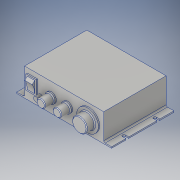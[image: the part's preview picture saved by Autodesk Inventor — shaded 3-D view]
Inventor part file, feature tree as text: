
AUTODESK INVENTOR PART (.ipt)
format: ipt  version: 2017 (Build 210142000, 142)  size: 264,192 bytes
history: native  units: in
note: dims shown in document units (in); Inventor stores cm internally (conversion verified against a paired STEP export)
features: projected_geometry x11, extrude x8, sketch x8, chamfer x2, plane x2, fillet x1
ambient origin geometry x8: Origin, YZ Plane, XZ Plane, XY Plane, X Axis, Y Axis, Z Axis, Center Point
bodies: Solid1 (feature_tree)
feature tree (32):
  extrude  "Extrusion1"  Depth=5.5118in
  extrude  "Extrusion2"  Depth=4.6063in
  fillet  "Fillet1"  Radius=1.5354in
  extrude  "Extrusion3"  Depth=1.2598in
  extrude  "Extrusion4"  Depth=0.5906in
  extrude  "Extrusion5"  Depth=0.5906in
  extrude  "Extrusion6"  Depth=0.1575in
  chamfer  "Chamfer1"  Distance=0.7874in
  chamfer  "Chamfer2"  Distance=0.5118in
  plane  "Work Plane1"
  plane  "Work Plane2"
  extrude  "Extrusion7"  Depth=1.2598in
  extrude  "Extrusion8"  Depth=0.5118in
  sketch  "Sketch1"  dims[d0=3.622in d1=5.5118in]
  sketch  "Sketch2"  dims[d2=0.0787in d3=0.0in d4=4.6063in d5=1.5354in d6=0.0in]
  projected_geometry  "Projected Loop1"
  sketch  "Sketch3"  dims[d7=0.0787in d8=1.2598in]
  projected_geometry  "Projected Loop2"
  sketch  "Sketch4"  dims[d9=0.5906in d10=0.5906in]
  projected_geometry  "Projected Loop3"
  projected_geometry  "Projected Loop4"
  projected_geometry  "Projected Loop5"
  projected_geometry  "Projected Loop6"
  sketch  "Sketch5"  dims[d11=0.2756in d12=0.5906in]
  projected_geometry  "Projected Loop7"
  sketch  "Sketch6"  dims[d13=0.8268in d14=0.1575in]
  projected_geometry  "Projected Loop8"
  sketch  "Sketch7"  dims[d15=0.2756in]
  projected_geometry  "Projected Loop9"
  sketch  "Sketch8"  dims[d17=0.3937in d18=0.7874in d19=0.5118in d20=1.2598in d21=0.5118in d22=2.2047in d23=0.1575in d24=0.2362in d25=0.0787in d26=0.0in d27=0.4921in d28=0.4921in d30=0.4921in d31=0.6181in d32=0.0in d33=0.8543in d34=0.5512in d35=0.0in d36=0.2598in d37=0.0in d38=0.0492in d39=0.0787in d40=45.0deg d41=0.0394in d42=0.0787in d43=45.0deg d44=-0.0787in d45=-0.0787in d46=0.0787in d47=0.0787in d48=45.0deg d49=0.1417in d50=0.2598in d51=0.0in d52=0.1693in d54=0.1693in d55=0.1693in d56=0.2756in d58=0.2756in d59=0.2756in d63=0.2598in d64=0.0in d66=0.1693in d67=0.2756in d68=0.9114in d69=0.9114in d70=0.9114in d71=0.9114in]
  projected_geometry  "Projected Loop10"
  projected_geometry  "Projected Loop11"
